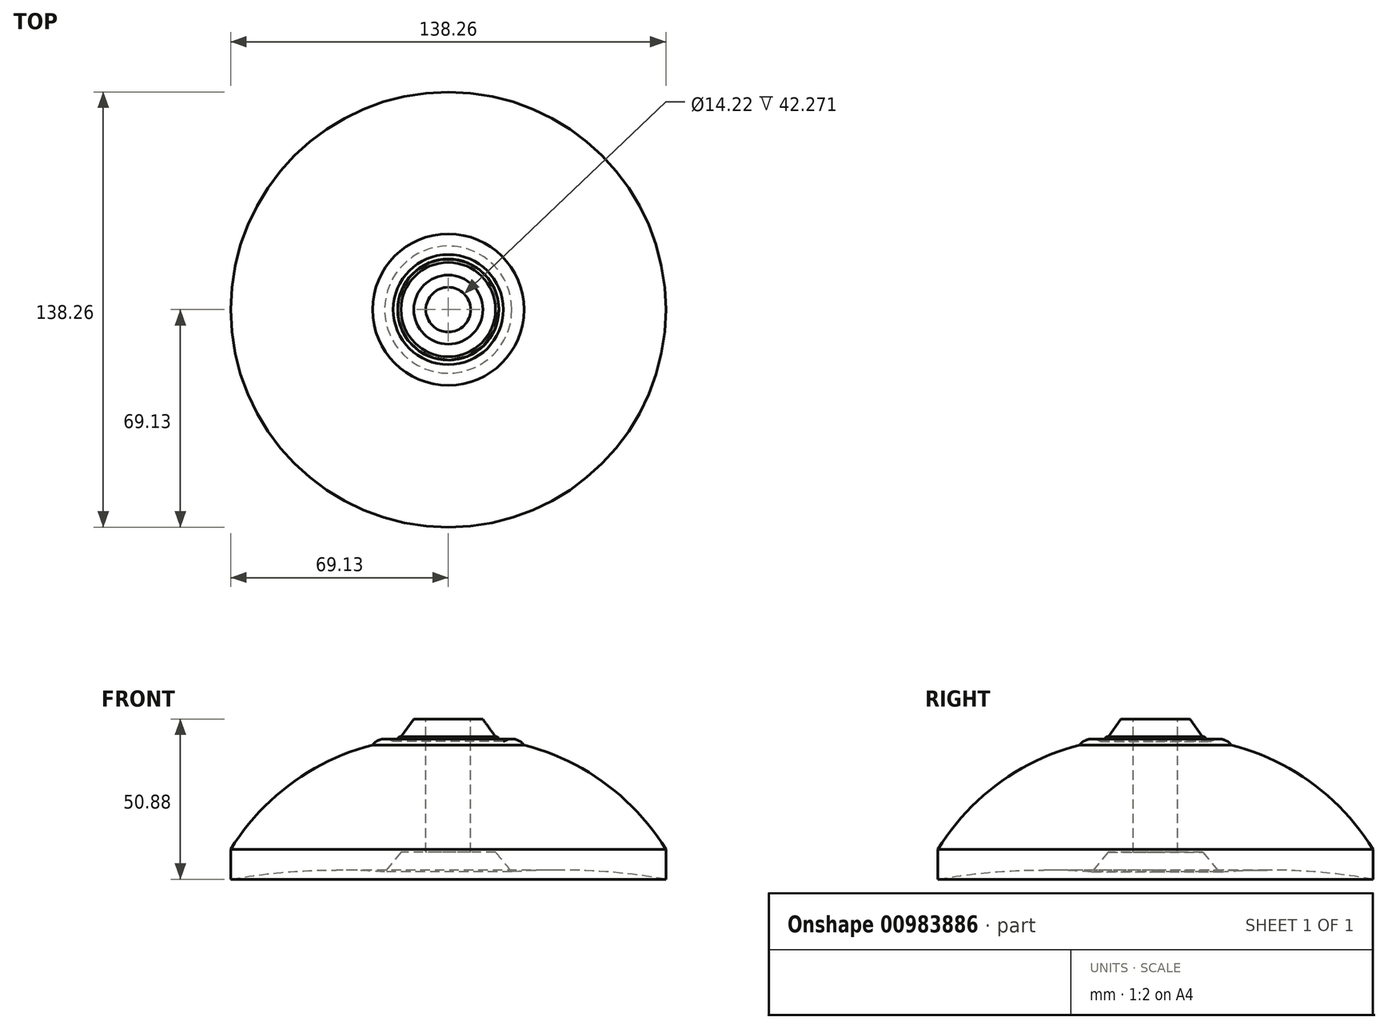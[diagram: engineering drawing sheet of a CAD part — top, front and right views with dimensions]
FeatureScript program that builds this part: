
annotation { "Feature Type Name" : "Feature", "Feature Type Description" : "" }
export const myFeature = defineFeature(function(context is Context, id is Id, definition is map)
    precondition{}
    {
        {
            var Q0;
            Q0=qCreatedBy(makeId("Right.planeOp"),FACE);
            var sketch = newSketch(context, id + "F0", { "sketchPlane" : qUnion([Q0])});
            skLineSegment(sketch, "E0", {"start": v(0, 0) * mm, "end": v(0, 31.27) * mm});
            skLineSegment(sketch, "E1", {"start": v(0, 31.27) * mm, "end": v(0, 0) * mm});
            skLineSegment(sketch, "E2", {"start": v(0, 0) * mm, "end": v(7.11, 0) * mm});
            skLineSegment(sketch, "E3", {"start": v(7.11, 0) * mm, "end": v(7.11, 38.1) * mm});
            skLineSegment(sketch, "E4.MirrorCS", {"start": v(7.11, 0) * mm, "end": v(7.11, -38.1) * mm});
            skLineSegment(sketch, "E5", {"start": v(7.11, 38.1) * mm, "end": v(10.97, 38.1) * mm});
            skLineSegment(sketch, "E6", {"start": v(10.97, 38.1) * mm, "end": v(15, 32.48) * mm});
            skArc(sketch, "E7", {"start": v(16.07, 31.63) * mm, "mid": v(15.76, 32.33) * mm, "end": v(15, 32.48) * mm});
            skArc(sketch, "E8", {"start": v(17.49, 30.94) * mm, "mid": v(16.8, 31.34) * mm, "end": v(16.07, 31.63) * mm});
            skArc(sketch, "E9", {"start": v(24.07, 29.87) * mm, "mid": v(21, 31.74) * mm, "end": v(17.49, 30.94) * mm});
            skArc(sketch, "E10", {"start": v(69.13, -3.26) * mm, "mid": v(49.81, 17.67) * mm, "end": v(24.07, 29.87) * mm});
            skLineSegment(sketch, "E11", {"start": v(69.13, -3.26) * mm, "end": v(69.13, -12.78) * mm});
            skArc(sketch, "E12", {"start": v(69.13, -12.78) * mm, "mid": v(44.74, -10.06) * mm, "end": v(20.2, -10.45) * mm});
            skLineSegment(sketch, "E13", {"start": v(20.2, -10.45) * mm, "end": v(15.03, -4.17) * mm});
            skLineSegment(sketch, "E14", {"start": v(15.03, -4.17) * mm, "end": v(7.11, -4.17) * mm});
            skSolve(sketch);
        }
        {
            var Q0;
            {var subQ0=sQuery(id+"F0.wireOp",EDGE,"E3");Q0=makeQuery(id+"F0.imprint","IMPRINT",FACE,{"disambiguationData":[TD([[makeQuery(id+"F0.imprint","IMPRINT",EDGE,{"derivedFrom":subQ0}),-1.0]])]});}
            var Q1;
            Q1=sQuery(id+"F0.wireOp",EDGE,"E1");
            revolve(context, id + "F1", {"surfaceOperationType" : NewSurfaceOperationType.NEW, "entities" : qUnion([Q0]), "axis" : qUnion([Q1]), "revolveType" : RevolveType.FULL});
        }
    });
